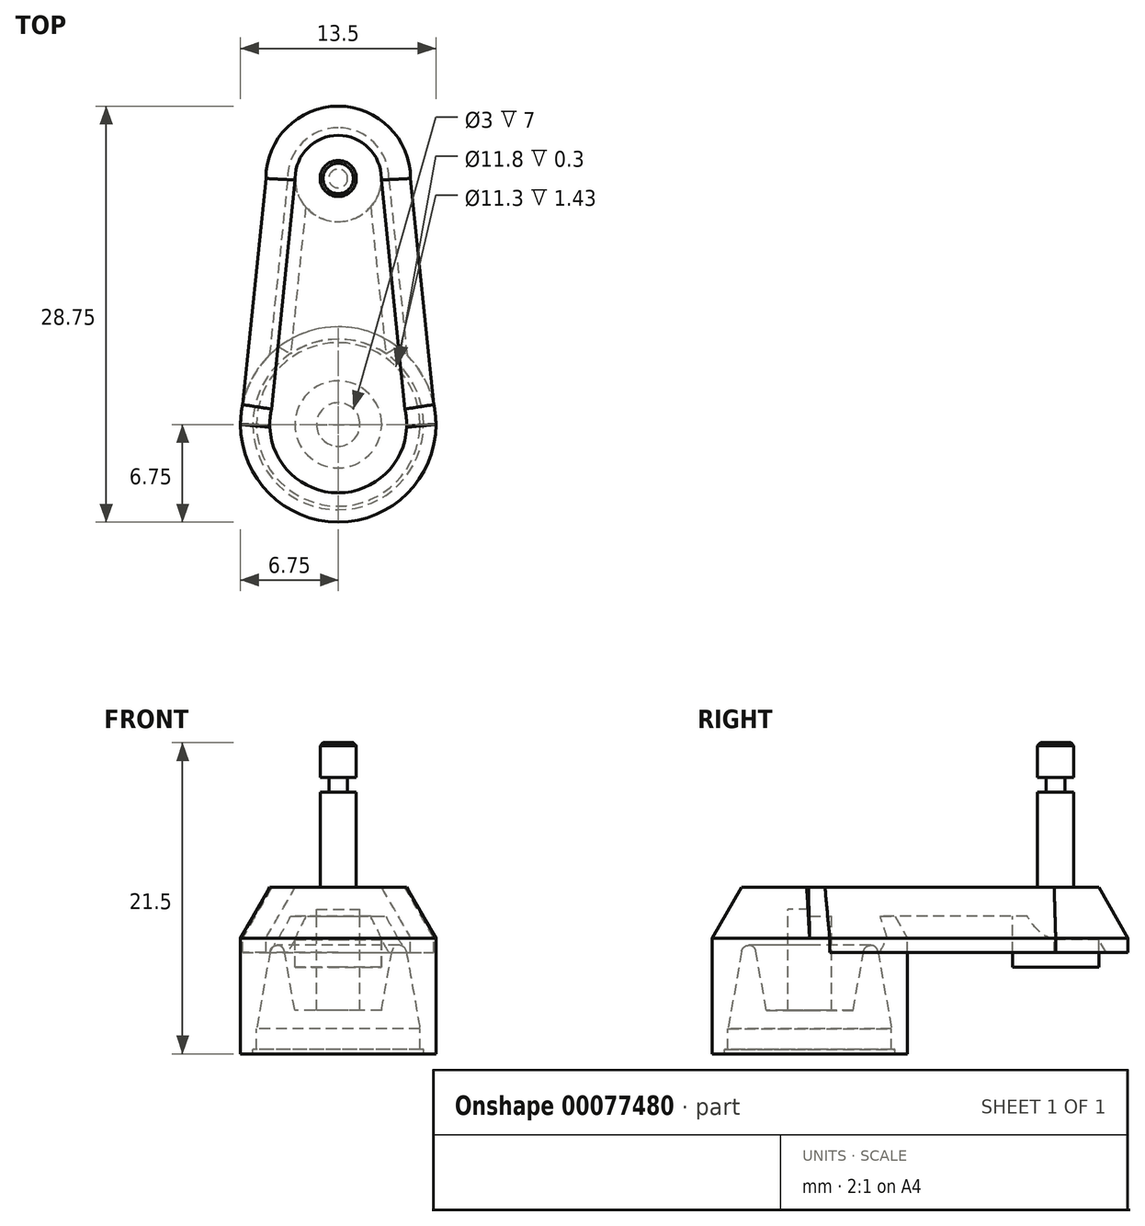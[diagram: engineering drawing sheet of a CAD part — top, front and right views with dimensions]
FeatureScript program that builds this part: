
annotation { "Feature Type Name" : "Feature", "Feature Type Description" : "" }
export const myFeature = defineFeature(function(context is Context, id is Id, definition is map)
    precondition{}
    {
        {
            var Q0;
            Q0=qCreatedBy(makeId("Right.planeOp"),FACE);
            var sketch = newSketch(context, id + "F0", { "sketchPlane" : qUnion([Q0])});
            skPoint(sketch, "E0", {"position": v(0, 11.5) * mm});
            skPoint(sketch, "E1", {"position": v(0, 10) * mm});
            skLineSegment(sketch, "E2", {"start": v(0, 10) * mm, "end": v(-1.5, 10) * mm});
            skLineSegment(sketch, "E3", {"start": v(-1.5, 10) * mm, "end": v(-1.5, 3) * mm});
            skLineSegment(sketch, "E4", {"start": v(-1.5, 3) * mm, "end": v(-3, 3) * mm});
            skLineSegment(sketch, "E5", {"start": v(-3, 3) * mm, "end": v(-3.72, 7.09) * mm});
            skLineSegment(sketch, "E6", {"start": v(-4.7, 7.09) * mm, "end": v(-5.65, 1.73) * mm});
            skLineSegment(sketch, "E7", {"start": v(-5.65, 1.73) * mm, "end": v(-5.65, 0.3) * mm});
            skLineSegment(sketch, "E8", {"start": v(-5.65, 0.3) * mm, "end": v(-5.9, 0.3) * mm});
            skLineSegment(sketch, "E9", {"start": v(-5.9, 0.3) * mm, "end": v(-5.9, 0) * mm});
            skLineSegment(sketch, "E10", {"start": v(-5.9, 0) * mm, "end": v(-6.75, 0) * mm});
            skLineSegment(sketch, "E11", {"start": v(-6.75, 0) * mm, "end": v(-6.75, 8) * mm});
            skLineSegment(sketch, "E12", {"start": v(-6.75, 8) * mm, "end": v(-4.73, 11.5) * mm});
            skLineSegment(sketch, "E13", {"start": v(-4.73, 11.5) * mm, "end": v(0, 11.5) * mm});
            skLineSegment(sketch, "E14", {"start": v(-5.65, 1.73) * mm, "end": v(-5.65, 11.5) * mm, "construction": true});
            skLineSegment(sketch, "E15", {"start": v(-3, 3) * mm, "end": v(-3, 11.5) * mm, "construction": true});
            skPoint(sketch, "E16.visualSharp", {"position": v(-4.21, 9.88) * mm});
            skArc(sketch, "E16.filletArc", {"start": v(-3.72, 7.09) * mm, "mid": v(-4.21, 7.5) * mm, "end": v(-4.7, 7.09) * mm});
            skLineSegment(sketch, "E17", {"start": v(-6.75, 8) * mm, "end": v(-6.75, 11.5) * mm, "construction": true});
            skLineSegment(sketch, "E18", {"start": v(0, 11.5) * mm, "end": v(0, 10) * mm});
            skSolve(sketch);
        }
        {
            var Q0;
            Q0=makeQuery(id+"F0.imprint","IMPRINT",FACE,{"disambiguationData":[TD([[makeQuery(id+"F0.imprint","IMPRINT",EDGE,{"derivedFrom":sQuery(id+"F0.wireOp",EDGE,"E2")}),-1.0]])]});
            var Q1;
            Q1=sQuery(id+"F0.wireOp",EDGE,"E18");
            revolve(context, id + "F1", {"entities" : qUnion([Q0]), "axis" : qUnion([Q1]), "revolveType" : RevolveType.FULL});
        }
        {
            var Q0;
            Q0=qCreatedBy(makeId("Right.planeOp"),FACE);
            var sketch = newSketch(context, id + "F2", { "sketchPlane" : qUnion([Q0])});
            skLineSegment(sketch, "E19", {"start": v(0, 0) * mm, "end": v(17, 0) * mm, "construction": true});
            skLineSegment(sketch, "E20", {"start": v(17, 0) * mm, "end": v(17, 11.5) * mm, "construction": true});
            skPoint(sketch, "E21", {"position": v(17, 9.5) * mm});
            skLineSegment(sketch, "E22", {"start": v(20.5, 7) * mm, "end": v(22, 7) * mm});
            skLineSegment(sketch, "E23", {"start": v(22, 7) * mm, "end": v(22, 8) * mm});
            skLineSegment(sketch, "E24", {"start": v(22, 8) * mm, "end": v(19.98, 11.5) * mm});
            skLineSegment(sketch, "E25", {"start": v(19.98, 11.5) * mm, "end": v(17, 11.5) * mm});
            skLineSegment(sketch, "E26", {"start": v(17, 9.5) * mm, "end": v(17, 11.5) * mm});
            skLineSegment(sketch, "E27", {"start": v(20.5, 7) * mm, "end": v(20.5, 0) * mm, "construction": true});
            skLineSegment(sketch, "E28", {"start": v(20.5, 7) * mm, "end": v(19.06, 9.5) * mm});
            skLineSegment(sketch, "E29", {"start": v(19.06, 9.5) * mm, "end": v(17, 9.5) * mm});
            skSolve(sketch);
        }
        {
            var Q0;
            Q0=qCreatedBy(makeId("Top.planeOp"),FACE);
            cPlane(context, id + "F3", {"entities" : qUnion([Q0]), "cplaneType" : CPlaneType.OFFSET, "offset" : 8 * mm, "width" : 150 * mm, "height" : 150 * mm});
        }
        {
            var Q0;
            Q0=qCreatedBy(id+"F3.planeOp",FACE);
            var sketch = newSketch(context, id + "F4", { "sketchPlane" : qUnion([Q0])});
            skArc(sketch, "E30", {"start": v(5, 17) * mm, "mid": v(3.54, 20.54) * mm, "end": v(0, 22) * mm});
            skPoint(sketch, "E31", {"position": v(0, 0) * mm});
            skLineSegment(sketch, "E32", {"start": v(-5, 17) * mm, "end": v(-6.75, 0) * mm});
            skLineSegment(sketch, "E33", {"start": v(5, 17) * mm, "end": v(6.75, 0) * mm});
            skLineSegment(sketch, "E34", {"start": v(0, 17) * mm, "end": v(0, 22) * mm, "construction": true});
            skLineSegment(sketch, "E35", {"start": v(0, 22) * mm, "end": v(0, 17) * mm, "construction": true});
            skArc(sketch, "E36", {"start": v(0, 22) * mm, "mid": v(-3.54, 20.54) * mm, "end": v(-5, 17) * mm});
            skSolve(sketch);
        }
        {
            var Q0;
            Q0=makeQuery(id+"F2.imprint","IMPRINT",FACE,{"disambiguationData":[TD([[makeQuery(id+"F2.imprint","IMPRINT",EDGE,{"derivedFrom":sQuery(id+"F2.wireOp",EDGE,"E22")}),1.0]])]});
            var Q1;
            Q1=sQuery(id+"F4.wireOp",EDGE,"E30");
            var Q2;
            Q2=sQuery(id+"F4.wireOp",EDGE,"E33");
            sweep(context, id + "F5", {"operationType" : NewBodyOperationType.ADD, "profiles" : qUnion([Q0]), "path" : qUnion([Q1, Q2])});
        }
        {
            var Q0;
            Q0=makeQuery(id+"F2.imprint","IMPRINT",FACE,{"disambiguationData":[TD([[makeQuery(id+"F2.imprint","IMPRINT",EDGE,{"derivedFrom":sQuery(id+"F2.wireOp",EDGE,"E22")}),1.0]])]});
            var Q1;
            Q1=sQuery(id+"F4.wireOp",EDGE,"E36");
            var Q2;
            Q2=sQuery(id+"F4.wireOp",EDGE,"E32");
            sweep(context, id + "F6", {"operationType" : NewBodyOperationType.ADD, "profiles" : qUnion([Q0]), "path" : qUnion([Q1, Q2])});
        }
        {
            var Q0;
            Q0=qCreatedBy(makeId("Front.planeOp"),FACE);
            var sketch = newSketch(context, id + "F7", { "sketchPlane" : qUnion([Q0])});
            skLineSegment(sketch, "E37.bottom", {"start": v(-2.5, 11.5) * mm, "end": v(2.5, 11.5) * mm});
            skLineSegment(sketch, "E37.top", {"start": v(-2.5, 9.5) * mm, "end": v(2.5, 9.5) * mm});
            skLineSegment(sketch, "E37.left", {"start": v(-2.5, 11.5) * mm, "end": v(-2.5, 9.5) * mm});
            skLineSegment(sketch, "E37.right", {"start": v(2.5, 11.5) * mm, "end": v(2.5, 9.5) * mm});
            skSolve(sketch);
        }
        {
            var Q0;
            Q0=makeQuery(id+"F7.imprint","IMPRINT",FACE,{"disambiguationData":[TD([[makeQuery(id+"F7.imprint","IMPRINT",EDGE,{"derivedFrom":sQuery(id+"F7.wireOp",EDGE,"E37.bottom")}),-1.0]])]});
            extrude(context, id + "F8", {"entities" : qUnion([Q0]), "operationType" : NewBodyOperationType.ADD, "oppositeDirection" : true, "depth" : 17 * mm});
        }
        {
            var Q0;
            {var subQ0=sQuery(id+"F2.wireOp",EDGE,"E25");Q0=makeQuery(id+"F8.boolean.opBoolean","MERGE",FACE,{"derivedFrom":[makeQuery(id+"F6.boolean.opBoolean","MERGE",FACE,{"derivedFrom":[makeQuery(id+"F5.boolean.opBoolean","MERGE",FACE,{"derivedFrom":[makeQuery(id+"F1.opRevolve","SWEPT_FACE",FACE,{"disambiguationData":[OSD([sQuery(id+"F0.wireOp",EDGE,"E13")])]}),makeQuery(id+"F5.opSweep","MID_CAP_FACE",FACE,{"disambiguationData":[OSD([subQ0,sQuery(id+"F4.wireOp",VERTEX,"E33.start")])],"capPos":1.0})]}),makeQuery(id+"F6.opSweep","MID_CAP_FACE",FACE,{"disambiguationData":[OSD([subQ0,sQuery(id+"F4.wireOp",VERTEX,"E32.start")])],"capPos":1.0})]}),makeQuery(id+"F8.opExtrude","SWEPT_FACE",FACE,{"disambiguationData":[OSD([sQuery(id+"F7.wireOp",EDGE,"E37.bottom")])]})]});}
            var sketch = newSketch(context, id + "F9", { "sketchPlane" : qUnion([Q0])});
            skLineSegment(sketch, "E38", {"start": v(0, 0) * mm, "end": v(0, 17) * mm, "construction": true});
            skCircle(sketch, "E39", {"center": v(0, 17) * mm, "radius": 2.98 * mm});
            skCircle(sketch, "E40", {"center": v(0, 17) * mm, "radius": 1.25 * mm});
            skSolve(sketch);
        }
        {
            var Q0;
            {var subQ0=sQuery(id+"F2.wireOp",EDGE,"E24");var subQ1=sQuery(id+"F2.wireOp",EDGE,"E25");var subQ2=sQuery(id+"F4.wireOp",EDGE,"E36");var subQ3=makeQuery(id+"F6.opSweep","SWEPT_EDGE",EDGE,{"disambiguationData":[OSD([subQ0,subQ1,subQ2]),OD(1.0)]});var subQ4=makeQuery(id+"F9.imprint","IMPRINT",EDGE,{"derivedFrom":subQ3});var subQ12=sQuery(id+"F4.wireOp",EDGE,"E30");var subQ13=makeQuery(id+"F5.opSweep","SWEPT_EDGE",EDGE,{"disambiguationData":[OSD([subQ0,subQ1,subQ12]),OD(1.0)]});var subQ14=makeQuery(id+"F9.imprint","IMPRINT",EDGE,{"derivedFrom":subQ13});Q0=qUnion([makeQuery(id+"F9.imprint","IMPRINT",FACE,{"disambiguationData":[TD([[subQ4,-1.0]])]}),makeQuery(id+"F9.imprint","IMPRINT",FACE,{"disambiguationData":[TD([[subQ14,1.0]])]}),makeQuery(id+"F9.imprint","IMPRINT",FACE,{"disambiguationData":[TD([[makeQuery(id+"F9.imprint","IMPRINT",EDGE,{"derivedFrom":sQuery(id+"F9.wireOp",EDGE,"E40")}),-1.0]])]})]);}
            var Q1;
            Q1=makeQuery(id+"F9.imprint","IMPRINT",FACE,{"disambiguationData":[TD([[makeQuery(id+"F9.imprint","IMPRINT",EDGE,{"derivedFrom":sQuery(id+"F9.wireOp",EDGE,"E40")}),1.0]])]});
            extrude(context, id + "F10", {"entities" : qUnion([Q0, Q1]), "operationType" : NewBodyOperationType.ADD, "oppositeDirection" : true, "depth" : 5.5 * mm});
        }
        {
            var Q0;
            Q0=makeQuery(id+"F9.imprint","IMPRINT",FACE,{"disambiguationData":[TD([[makeQuery(id+"F9.imprint","IMPRINT",EDGE,{"derivedFrom":sQuery(id+"F9.wireOp",EDGE,"E40")}),1.0]])]});
            extrude(context, id + "F11", {"entities" : qUnion([Q0]), "operationType" : NewBodyOperationType.ADD, "depth" : 6.6 * mm});
        }
        {
            var Q0;
            Q0=makeQuery(id+"F11.opExtrude","CAP_FACE",FACE,{"disambiguationData":[OSD([sQuery(id+"F9.wireOp",EDGE,"E40")])],"isStart":false});
            var sketch = newSketch(context, id + "F12", { "sketchPlane" : qUnion([Q0])});
            skCircle(sketch, "E41", {"center": v(0, 17) * mm, "radius": 0.65 * mm});
            skSolve(sketch);
        }
        {
            var Q0;
            Q0=makeQuery(id+"F12.imprint","IMPRINT",FACE,{"disambiguationData":[TD([[makeQuery(id+"F12.imprint","IMPRINT",EDGE,{"derivedFrom":sQuery(id+"F12.wireOp",EDGE,"E41")}),1.0]])]});
            extrude(context, id + "F13", {"entities" : qUnion([Q0]), "operationType" : NewBodyOperationType.ADD, "depth" : 1 * mm});
        }
        {
            var Q0;
            Q0=makeQuery(id+"F13.opExtrude","CAP_FACE",FACE,{"disambiguationData":[OSD([sQuery(id+"F12.wireOp",EDGE,"E41")])],"isStart":false});
            var sketch = newSketch(context, id + "F14", { "sketchPlane" : qUnion([Q0])});
            skCircle(sketch, "E42", {"center": v(0, 17) * mm, "radius": 1.25 * mm});
            skSolve(sketch);
        }
        {
            var Q0;
            {var subQ0=makeQuery(id+"F14.imprint","IMPRINT",EDGE,{"derivedFrom":makeQuery(id+"F13.opExtrude","CAP_EDGE",EDGE,{"disambiguationData":[OSD([sQuery(id+"F12.wireOp",EDGE,"E41")])],"isStart":false})});Q0=qUnion([makeQuery(id+"F14.imprint","IMPRINT",FACE,{"disambiguationData":[TD([[makeQuery(id+"F14.imprint","IMPRINT",EDGE,{"derivedFrom":sQuery(id+"F14.wireOp",EDGE,"E42")}),1.0]])]}),makeQuery(id+"F14.imprint","IMPRINT",FACE,{"disambiguationData":[TD([[subQ0,1.0]])]})]);}
            extrude(context, id + "F15", {"entities" : qUnion([Q0]), "operationType" : NewBodyOperationType.ADD, "depth" : 2.4 * mm});
        }
        {
            var Q0;
            Q0=makeQuery(id+"F15.opExtrude","CAP_EDGE",EDGE,{"disambiguationData":[OSD([sQuery(id+"F14.wireOp",EDGE,"E42")])],"isStart":false});
            chamfer(context, id + "F16", {"entities" : qUnion([Q0]), "width" : 0.2 * mm, "tangentPropagation" : true});
        }
    });
